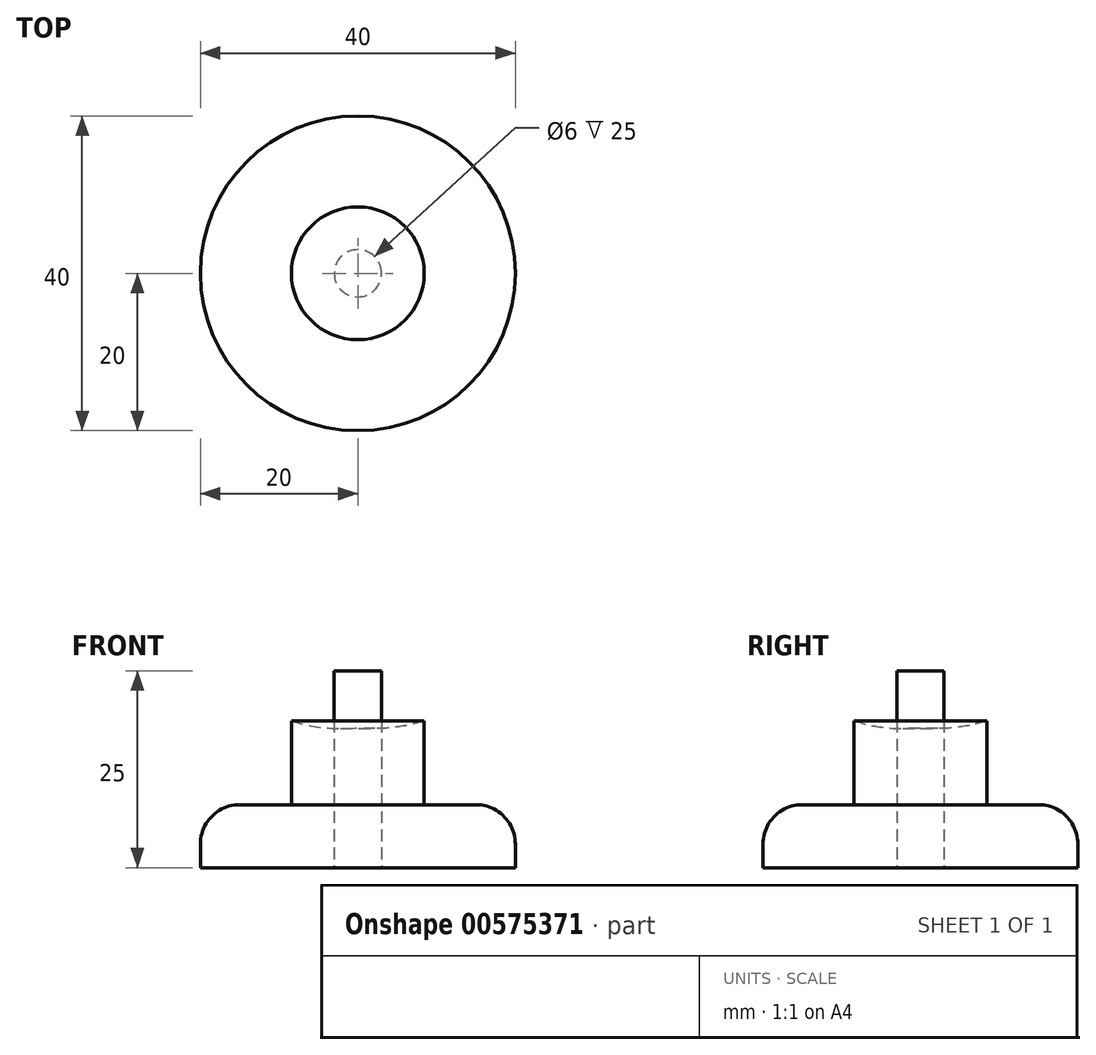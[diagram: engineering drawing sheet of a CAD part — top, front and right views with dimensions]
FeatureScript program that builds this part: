
annotation { "Feature Type Name" : "Feature", "Feature Type Description" : "" }
export const myFeature = defineFeature(function(context is Context, id is Id, definition is map)
    precondition{}
    {
        {
            var Q0;
            Q0=qCreatedBy(makeId("Top.planeOp"),FACE);
            var sketch = newSketch(context, id + "F0", { "sketchPlane" : qUnion([Q0])});
            skCircle(sketch, "E0", {"center": v(0, 0) * mm, "radius": 20 * mm});
            skSolve(sketch);
        }
        {
            var Q0;
            Q0 = qSketchRegion(id + "F0", true);
            extrude(context, id + "F1", {"entities" : qUnion([Q0]), "depth" : 8 * mm, "offsetDistance" : 25 * mm});
        }
        {
            var Q0;
            Q0=qCreatedBy(makeId("Front.planeOp"),FACE);
            var sketch = newSketch(context, id + "F2", { "sketchPlane" : qUnion([Q0])});
            skLineSegment(sketch, "E1", {"start": v(0, 7.68) * mm, "end": v(0, 57.68) * mm});
            skArc(sketch, "E2", {"start": v(8.44, 18.66) * mm, "mid": v(21.81, 41.97) * mm, "end": v(0, 57.68) * mm});
            skLineSegment(sketch, "E3", {"start": v(8.44, 18.66) * mm, "end": v(8.44, 7.75) * mm});
            skLineSegment(sketch, "E4", {"start": v(0, 7.68) * mm, "end": v(8.44, 7.75) * mm});
            skSolve(sketch);
        }
        {
            var Q0;
            Q0=makeQuery(id+"F2.imprint","IMPRINT",FACE,{"disambiguationData":[TD([[makeQuery(id+"F2.imprint","IMPRINT",EDGE,{"derivedFrom":sQuery(id+"F2.wireOp",EDGE,"E1")}),-1.0]])]});
            var Q1;
            Q1=sQuery(id+"F2.wireOp",EDGE,"E1");
            revolve(context, id + "F3", {"operationType" : NewBodyOperationType.ADD, "entities" : qUnion([Q0]), "axis" : qUnion([Q1]), "revolveType" : RevolveType.FULL});
        }
        {
            var Q0;
            Q0=makeQuery(id+"F1.opExtrude","CAP_EDGE",EDGE,{"disambiguationData":[OSD([sQuery(id+"F0.wireOp",EDGE,"E0")])],"isStart":false});
            fillet(context, id + "F4", {"entities" : qUnion([Q0]), "radius" : 5 * mm, "tangentPropagation" : true, "allowEdgeOverflow" : false});
        }
        {
            var Q0;
            Q0=makeQuery(id+"F1.opExtrude","CAP_FACE",FACE,{"disambiguationData":[OSD([sQuery(id+"F0.wireOp",EDGE,"E0")])],"isStart":true});
            var sketch = newSketch(context, id + "F5", { "sketchPlane" : qUnion([Q0])});
            skCircle(sketch, "E5", {"center": v(0, 0) * mm, "radius": 3 * mm});
            skSolve(sketch);
        }
        {
            var Q0;
            Q0 = qSketchRegion(id + "F5", true);
            extrude(context, id + "F6", {"entities" : qUnion([Q0]), "operationType" : NewBodyOperationType.REMOVE, "oppositeDirection" : true, "depth" : 25 * mm, "offsetDistance" : 25 * mm});
        }
    });
